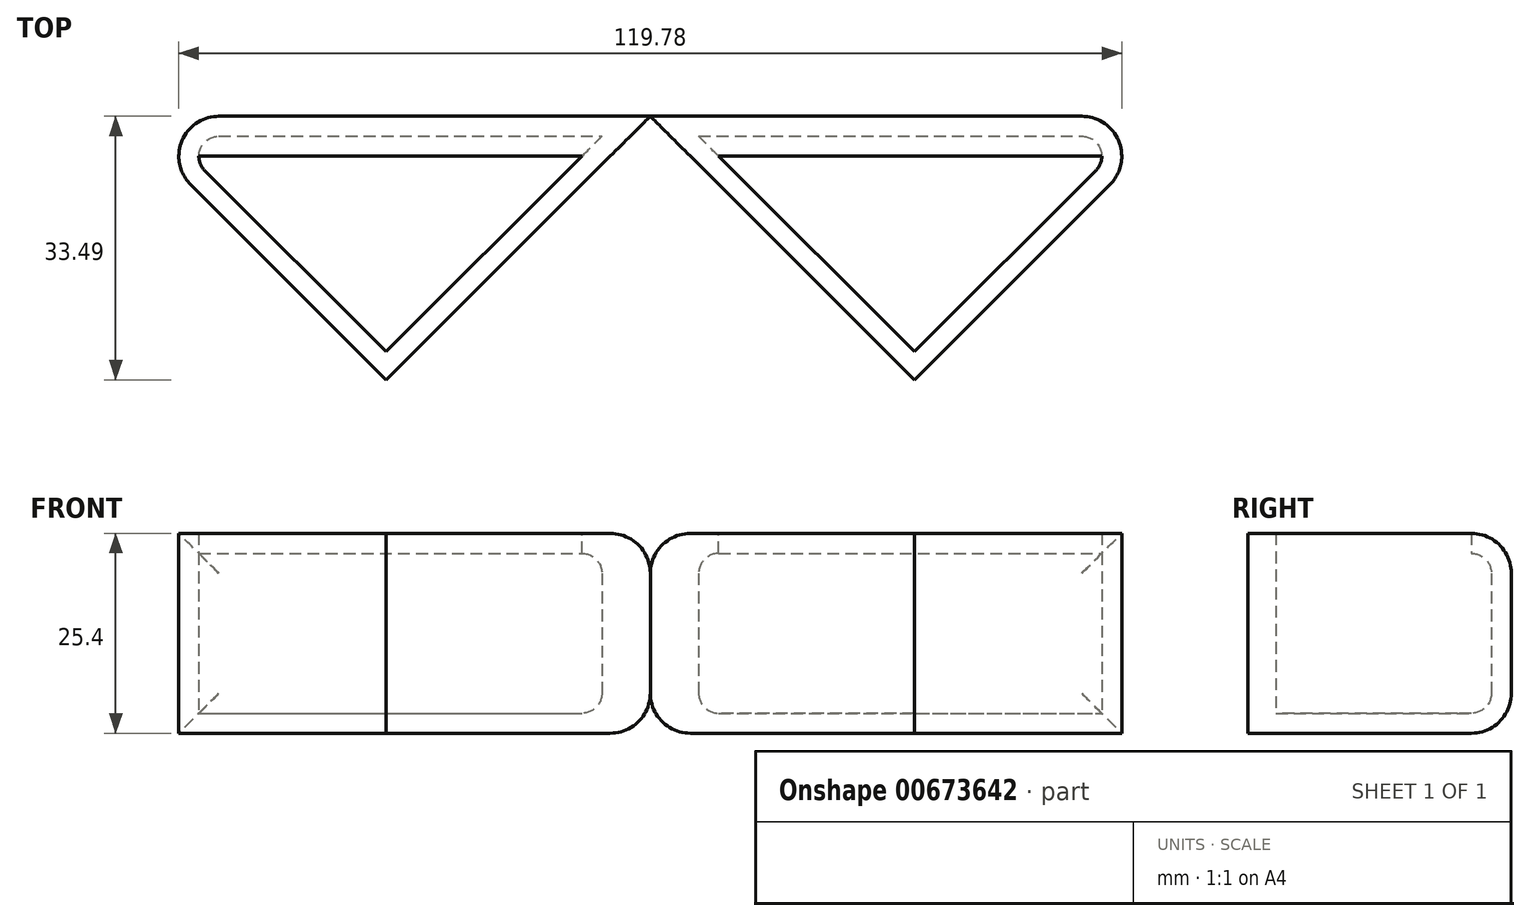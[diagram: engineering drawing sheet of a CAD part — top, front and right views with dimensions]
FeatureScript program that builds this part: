
annotation { "Feature Type Name" : "Feature", "Feature Type Description" : "" }
export const myFeature = defineFeature(function(context is Context, id is Id, definition is map)
    precondition{}
    {
        {
            var Q0;
            Q0=qCreatedBy(makeId("Top.planeOp"),FACE);
            var sketch = newSketch(context, id + "F0", { "sketchPlane" : qUnion([Q0])});
            skLineSegment(sketch, "E0.bottom", {"start": v(67.1, 66.97) * mm, "end": v(-67.1, 66.97) * mm});
            skLineSegment(sketch, "E0.top", {"start": v(67.1, -66.97) * mm, "end": v(-67.1, -66.97) * mm});
            skLineSegment(sketch, "E0.left", {"start": v(67.1, 66.97) * mm, "end": v(67.1, -66.97) * mm});
            skLineSegment(sketch, "E0.right", {"start": v(-67.1, 66.97) * mm, "end": v(-67.1, -66.97) * mm});
            skPoint(sketch, "E0.middle", {"position": v(0, 0) * mm});
            skLineSegment(sketch, "E1", {"start": v(0, -66.97) * mm, "end": v(0, 66.97) * mm});
            skLineSegment(sketch, "E2", {"start": v(-67.1, 0) * mm, "end": v(67.1, 0) * mm});
            skLineSegment(sketch, "E3", {"start": v(0, 0) * mm, "end": v(-67.1, -66.97) * mm});
            skLineSegment(sketch, "E4", {"start": v(-67.1, 0) * mm, "end": v(0, -66.97) * mm});
            skLineSegment(sketch, "E5", {"start": v(0, -66.97) * mm, "end": v(67.1, 0) * mm});
            skLineSegment(sketch, "E6", {"start": v(67.1, 0) * mm, "end": v(0, 66.97) * mm});
            skLineSegment(sketch, "E7", {"start": v(0, 0) * mm, "end": v(67.1, 66.97) * mm});
            skLineSegment(sketch, "E8", {"start": v(-67.1, 66.97) * mm, "end": v(67.1, -66.97) * mm});
            skLineSegment(sketch, "E9", {"start": v(-67.1, 0) * mm, "end": v(0, 66.97) * mm});
            skSolve(sketch);
        }
        {
            var Q0;
            Q0=makeQuery(id+"F0.imprint","IMPRINT",FACE,{"disambiguationData":[TD([[makeQuery(id+"F0.imprint","IMPRINT",EDGE,{"derivedFrom":sQuery(id+"F0.wireOp",EDGE,"E0.bottom")}),1.0]])]});
            extrude(context, id + "F1", {"entities" : qUnion([Q0]), "depth" : 25.4 * mm, "offsetDistance" : 25.4 * mm});
        }
        {
            var Q0;
            Q0=makeQuery(id+"F1.opExtrude","CAP_EDGE",EDGE,{"disambiguationData":[OSD([sQuery(id+"F0.wireOp",EDGE,"E0.bottom")])],"isStart":false});
            var Q1;
            Q1=makeQuery(id+"F1.opExtrude","CAP_EDGE",EDGE,{"disambiguationData":[OSD([sQuery(id+"F0.wireOp",EDGE,"E0.bottom")])],"isStart":true});
            var Q2;
            Q2=makeQuery(id+"F1.opExtrude","SWEPT_EDGE",EDGE,{"disambiguationData":[OSD([sQuery(id+"F0.wireOp",EDGE,"E0.bottom"),sQuery(id+"F0.wireOp",EDGE,"E0.left")])]});
            var Q3;
            Q3=makeQuery(id+"F1.opExtrude","SWEPT_EDGE",EDGE,{"disambiguationData":[OSD([sQuery(id+"F0.wireOp",EDGE,"E0.bottom"),sQuery(id+"F0.wireOp",EDGE,"E0.right")])]});
            fillet(context, id + "F2", {"entities" : qUnion([Q0, Q1, Q2, Q3]), "radius" : 5.08 * mm, "tangentPropagation" : true, "allowEdgeOverflow" : false});
        }
        {
            var Q0;
            Q0=makeQuery(id+"F1.opExtrude","CAP_FACE",FACE,{"disambiguationData":[OSD([sQuery(id+"F0.wireOp",EDGE,"E0.bottom"),sQuery(id+"F0.wireOp",EDGE,"E0.top"),sQuery(id+"F0.wireOp",EDGE,"E0.left"),sQuery(id+"F0.wireOp",EDGE,"E0.right")])],"isStart":false});
            shell(context, id + "F3", {"entities" : qUnion([Q0]), "thickness" : 2.54 * mm});
        }
    });
